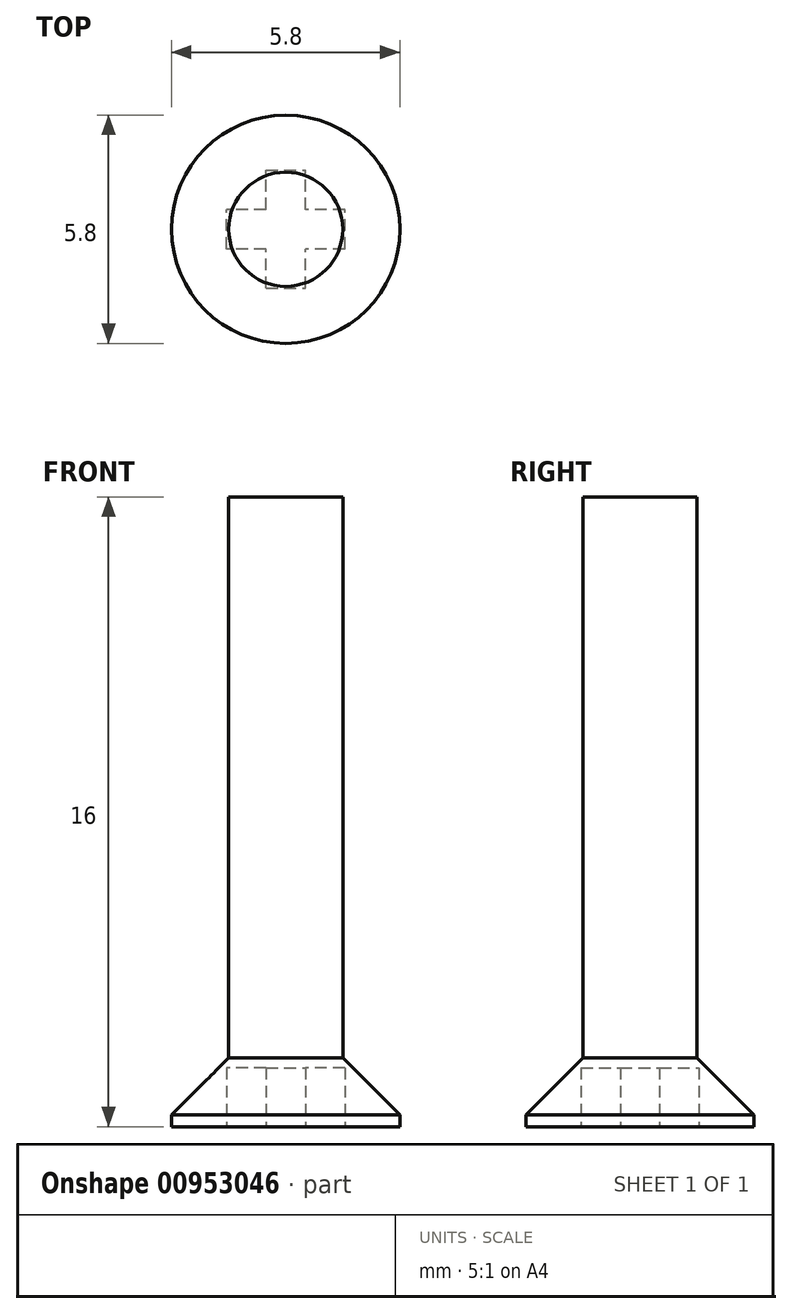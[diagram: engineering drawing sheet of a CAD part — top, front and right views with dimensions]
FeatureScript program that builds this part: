
annotation { "Feature Type Name" : "Feature", "Feature Type Description" : "" }
export const myFeature = defineFeature(function(context is Context, id is Id, definition is map)
    precondition{}
    {
        {
            var Q0;
            Q0=qCreatedBy(makeId("Top.planeOp"),FACE);
            var sketch = newSketch(context, id + "F0", { "sketchPlane" : qUnion([Q0])});
            skCircle(sketch, "E0", {"center": v(0, 0) * mm, "radius": 1.45 * mm});
            skSolve(sketch);
        }
        {
            var Q0;
            Q0=qSketchRegion(id+"F0",true);
            extrude(context, id + "F1", {"entities" : qUnion([Q0]), "offsetDistance" : 25 * mm, "depth" : (27.5 - 13.3) * mm});
        }
        {
            var Q0;
            Q0=qCreatedBy(makeId("Top.planeOp"),FACE);
            var sketch = newSketch(context, id + "F2", { "sketchPlane" : qUnion([Q0])});
            skCircle(sketch, "E1", {"center": v(0, 0) * mm, "radius": 2.9 * mm});
            skSolve(sketch);
        }
        {
            var Q0;
            Q0=qSketchRegion(id+"F2",true);
            extrude(context, id + "F3", {"entities" : qUnion([Q0]), "operationType" : NewBodyOperationType.ADD, "oppositeDirection" : true, "offsetDistance" : 25 * mm, "depth" : 1.8 * mm});
        }
        {
            var Q0;
            Q0=makeQuery(id+"F3.opExtrude","CAP_FACE",FACE,{"disambiguationData":[OSD([sQuery(id+"F2.wireOp",EDGE,"E1")])],"isStart":false});
            var sketch = newSketch(context, id + "F4", { "sketchPlane" : qUnion([Q0])});
            skLineSegment(sketch, "E2.bottom", {"start": v(1.5, 0.5) * mm, "end": v(-1.5, 0.5) * mm});
            skLineSegment(sketch, "E2.top", {"start": v(1.5, -0.5) * mm, "end": v(-1.5, -0.5) * mm});
            skLineSegment(sketch, "E2.left", {"start": v(1.5, 0.5) * mm, "end": v(1.5, -0.5) * mm});
            skLineSegment(sketch, "E2.right", {"start": v(-1.5, 0.5) * mm, "end": v(-1.5, -0.5) * mm});
            skPoint(sketch, "E2.middle", {"position": v(0, 0) * mm});
            skLineSegment(sketch, "E3.bottom", {"start": v(-0.5, 1.5) * mm, "end": v(0.5, 1.5) * mm});
            skLineSegment(sketch, "E3.top", {"start": v(-0.5, -1.5) * mm, "end": v(0.5, -1.5) * mm});
            skLineSegment(sketch, "E3.left", {"start": v(-0.5, 1.5) * mm, "end": v(-0.5, -1.5) * mm});
            skLineSegment(sketch, "E3.right", {"start": v(0.5, 1.5) * mm, "end": v(0.5, -1.5) * mm});
            skSolve(sketch);
        }
        {
            var Q0;
            Q0=qSketchRegion(id+"F4",true);
            extrude(context, id + "F5", {"entities" : qUnion([Q0]), "operationType" : NewBodyOperationType.REMOVE, "oppositeDirection" : true, "depth" : 1.5 * mm});
        }
        {
            var Q0;
            Q0=makeQuery(id+"F3.opExtrude","CAP_EDGE",EDGE,{"disambiguationData":[OSD([sQuery(id+"F2.wireOp",EDGE,"E1")])],"isStart":true});
            chamfer(context, id + "F6", {"entities" : qUnion([Q0]), "width" : 1.5 * mm, "tangentPropagation" : true});
        }
    });
